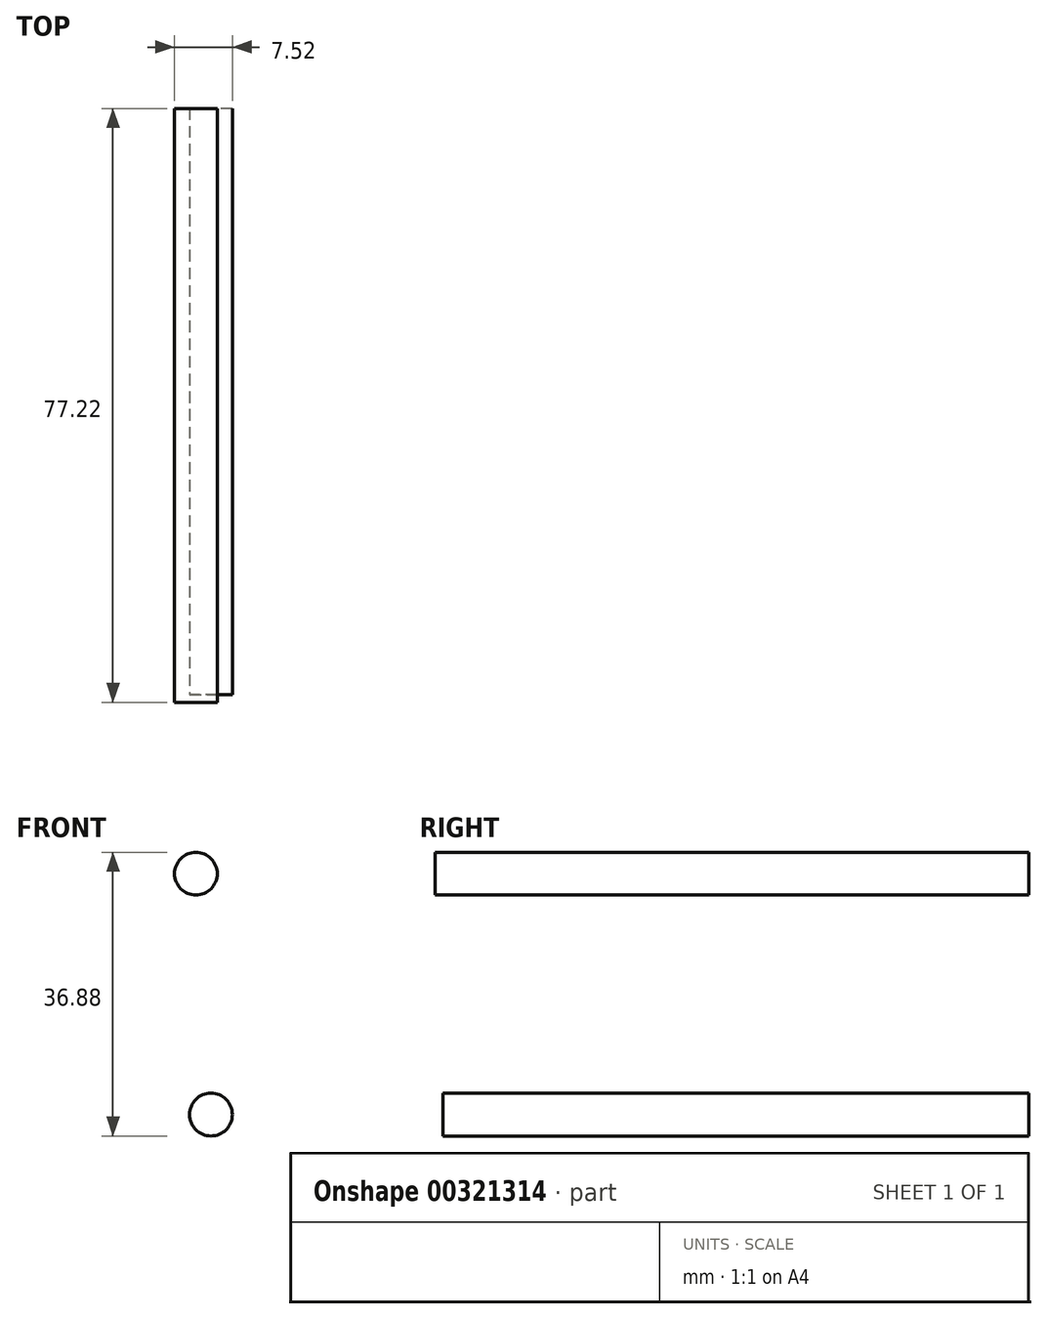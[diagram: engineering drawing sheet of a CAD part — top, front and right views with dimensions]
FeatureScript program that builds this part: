
annotation { "Feature Type Name" : "Feature", "Feature Type Description" : "" }
export const myFeature = defineFeature(function(context is Context, id is Id, definition is map)
    precondition{}
    {
        {
            var Q0;
            Q0=qCreatedBy(makeId("Front.planeOp"),FACE);
            var sketch = newSketch(context, id + "F0", { "sketchPlane" : qUnion([Q0])});
            skCircle(sketch, "E0", {"center": v(12.61, -31.32) * mm, "radius": 2.78 * mm});
            skCircle(sketch, "E1", {"center": v(10.65, 0) * mm, "radius": 2.78 * mm});
            skSolve(sketch);
        }
        {
            var Q0;
            Q0=sQuery(id+"F0.wireOp",EDGE,"E0");
            extrude(context, id + "F1", {"bodyType" : ToolBodyType.SURFACE, "surfaceEntities" : qUnion([Q0]), "depth" : 76.2 * mm});
        }
        {
            var Q0;
            Q0=sQuery(id+"F0.wireOp",EDGE,"E1");
            extrude(context, id + "F2", {"bodyType" : ToolBodyType.SURFACE, "surfaceEntities" : qUnion([Q0]), "depth" : 77.22 * mm});
        }
    });
